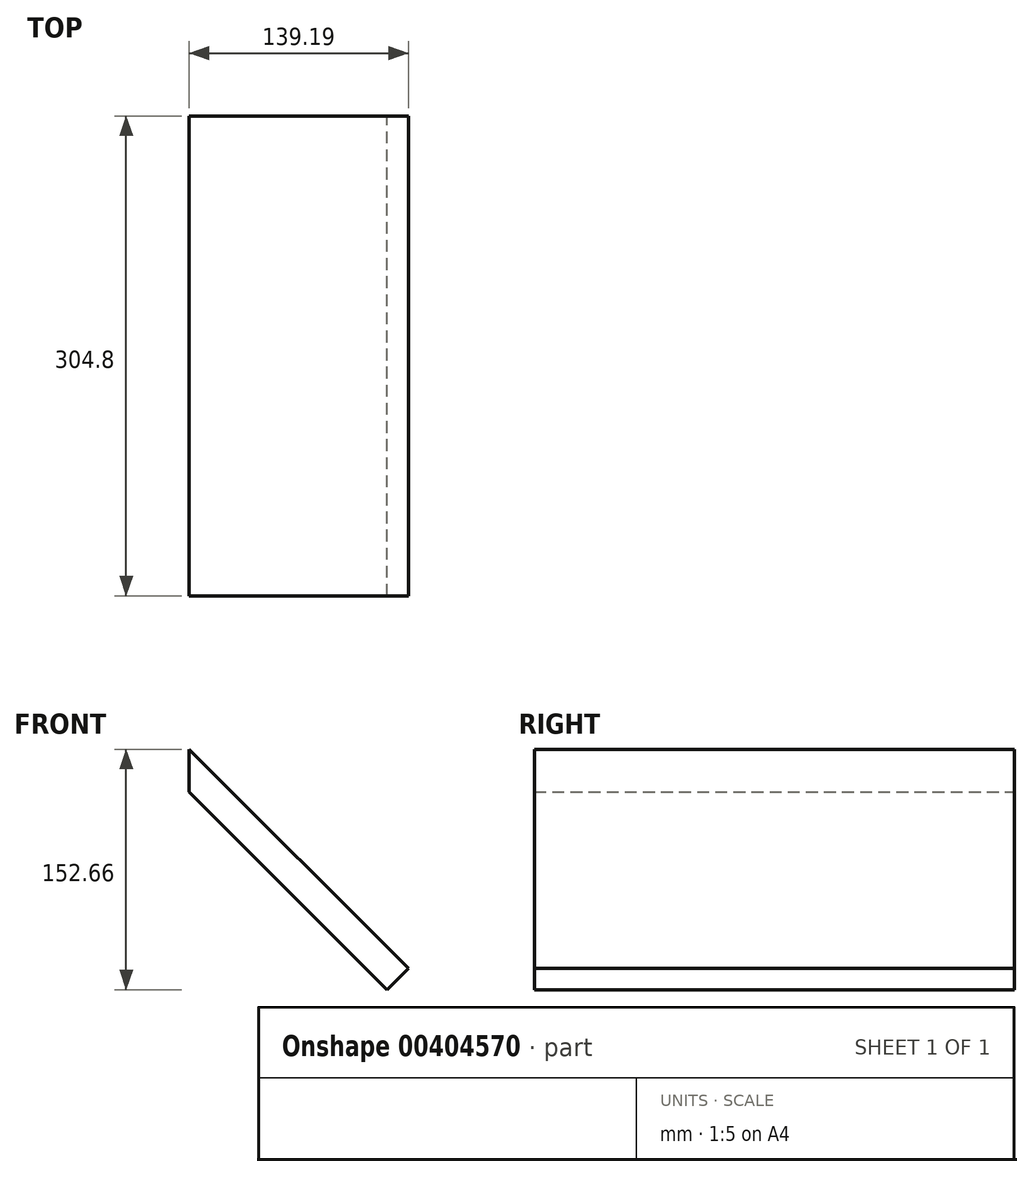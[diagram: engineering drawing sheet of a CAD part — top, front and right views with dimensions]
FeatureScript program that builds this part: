
annotation { "Feature Type Name" : "Feature", "Feature Type Description" : "" }
export const myFeature = defineFeature(function(context is Context, id is Id, definition is map)
    precondition{}
    {
        {
            var Q0;
            Q0=qCreatedBy(makeId("Front.planeOp"),FACE);
            var sketch = newSketch(context, id + "F0", { "sketchPlane" : qUnion([Q0])});
            skLineSegment(sketch, "E0.right", {"start": v(-341.41, 790.1) * mm, "end": v(-341.41, 817.04) * mm});
            skLineSegment(sketch, "E1.MirrorCS", {"start": v(-215.69, 664.38) * mm, "end": v(-341.41, 790.1) * mm});
            skLineSegment(sketch, "E2.MirrorCS", {"start": v(-202.22, 677.85) * mm, "end": v(-341.41, 817.04) * mm});
            skLineSegment(sketch, "E3", {"start": v(-202.22, 677.85) * mm, "end": v(-215.69, 664.38) * mm});
            skSolve(sketch);
        }
        {
            var Q0;
            Q0=qSketchRegion(id+"F0",true);
            extrude(context, id + "F1", {"entities" : qUnion([Q0]), "endBound" : BoundingType.SYMMETRIC, "depth" : 304.8 * mm});
        }
        {
            var Q0;
            Q0=makeQuery(id+"F1.opExtrude","SWEPT_FACE",FACE,{"disambiguationData":[OSD([sQuery(id+"F0.wireOp",EDGE,"E2.MirrorCS")])]});
            var sketch = newSketch(context, id + "F2", { "sketchPlane" : qUnion([Q0])});
            skLineSegment(sketch, "E4.bottom", {"start": v(-730.25, -152.4) * mm, "end": v(-711.2, -152.4) * mm});
            skLineSegment(sketch, "E4.top", {"start": v(-730.25, 0) * mm, "end": v(-711.2, 0) * mm});
            skLineSegment(sketch, "E4.left", {"start": v(-730.25, 0) * mm, "end": v(-730.25, -152.4) * mm});
            skLineSegment(sketch, "E4.right", {"start": v(-711.2, 0) * mm, "end": v(-711.2, -152.4) * mm});
            skSolve(sketch);
        }
        {
            var Q0;
            Q0=qSketchRegion(id+"F2",true);
            extrude(context, id + "F3", {"entities" : qUnion([Q0]), "operationType" : NewBodyOperationType.REMOVE, "oppositeDirection" : true, "depth" : 19.05 * mm});
        }
    });
